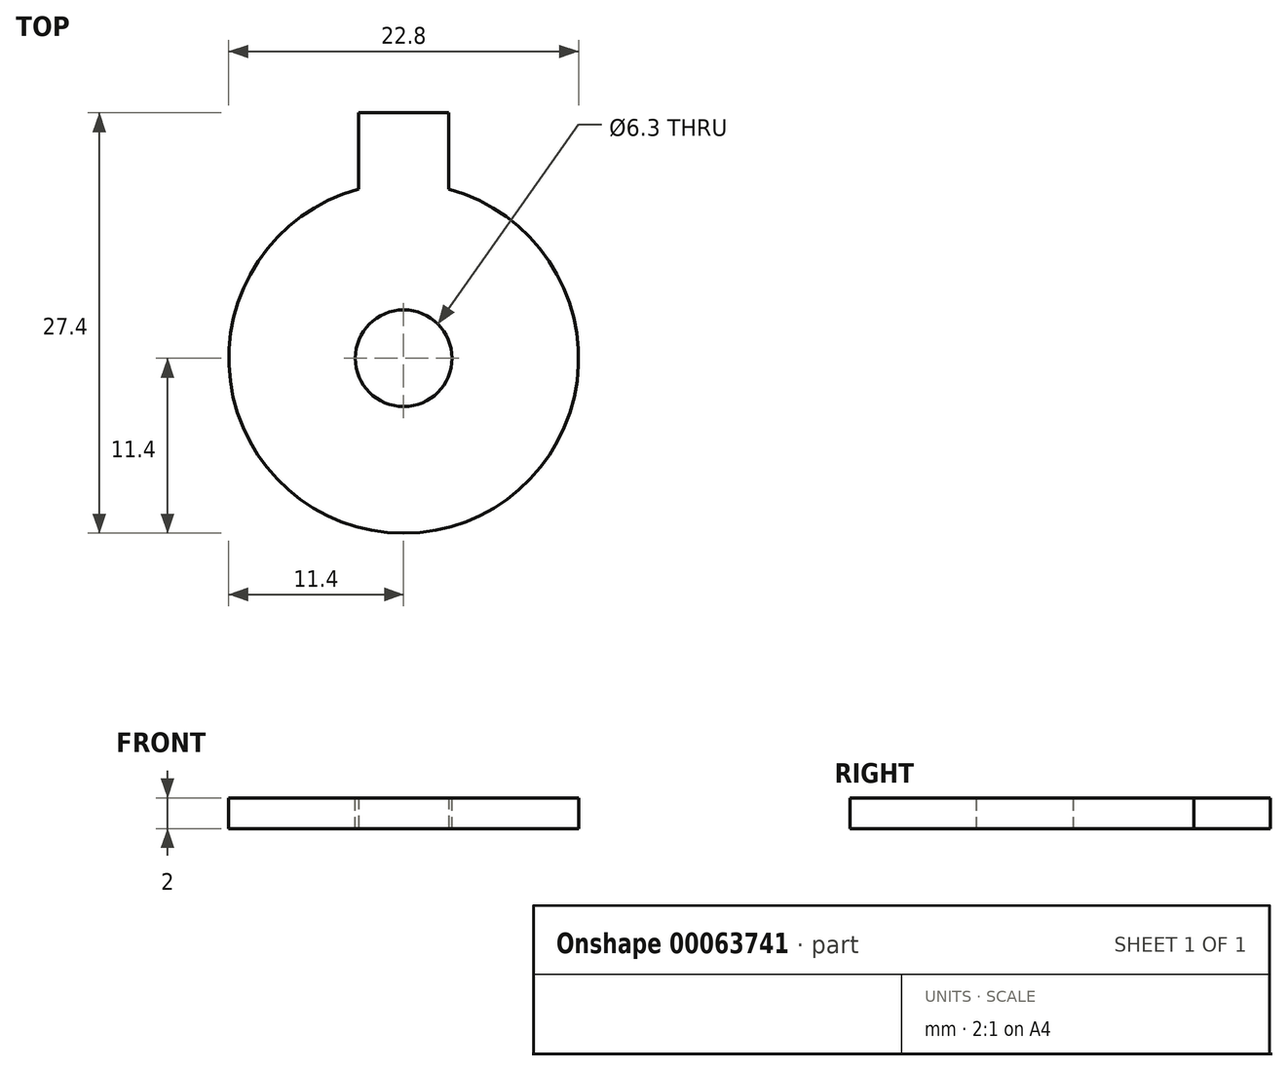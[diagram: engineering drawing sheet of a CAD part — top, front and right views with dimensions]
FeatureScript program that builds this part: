
annotation { "Feature Type Name" : "Feature", "Feature Type Description" : "" }
export const myFeature = defineFeature(function(context is Context, id is Id, definition is map)
    precondition{}
    {
        {
            var Q0;
            Q0=qCreatedBy(makeId("Top.planeOp"),FACE);
            var sketch = newSketch(context, id + "F0", { "sketchPlane" : qUnion([Q0])});
            skArc(sketch, "E0", {"start": v(-2.95, 11.01) * mm, "mid": v(0, -11.4) * mm, "end": v(2.95, 11.01) * mm});
            skLineSegment(sketch, "E1.rect.bottom", {"start": v(2.95, 16) * mm, "end": v(-2.95, 16) * mm});
            skLineSegment(sketch, "E1.rect.left", {"start": v(2.95, 16) * mm, "end": v(2.95, 11.01) * mm});
            skLineSegment(sketch, "E1.rect.right", {"start": v(-2.95, 16) * mm, "end": v(-2.95, 11.01) * mm});
            skPoint(sketch, "E1.rect.middle", {"position": v(0, 11.4) * mm});
            skPoint(sketch, "E1.rect.top.end.orphan", {"position": v(-2.95, 6.8) * mm});
            skPoint(sketch, "E2.orphan", {"position": v(2.95, 6.8) * mm});
            skSolve(sketch);
        }
        {
            var Q0;
            Q0=makeQuery(id+"F0.imprint","IMPRINT",FACE,{"disambiguationData":[TD([[makeQuery(id+"F0.imprint","IMPRINT",EDGE,{"derivedFrom":sQuery(id+"F0.wireOp",EDGE,"E0")}),1.0]])]});
            extrude(context, id + "F1", {"entities" : qUnion([Q0]), "depth" : 2 * mm});
        }
        {
            var Q0;
            Q0=makeQuery(id+"F1.opExtrude","CAP_FACE",FACE,{"disambiguationData":[OSD([sQuery(id+"F0.wireOp",EDGE,"E0"),sQuery(id+"F0.wireOp",EDGE,"E1.rect.bottom"),sQuery(id+"F0.wireOp",EDGE,"E1.rect.left"),sQuery(id+"F0.wireOp",EDGE,"E1.rect.right")])],"isStart":false});
            var sketch = newSketch(context, id + "F2", { "sketchPlane" : qUnion([Q0])});
            skCircle(sketch, "E3", {"center": v(0, 0) * mm, "radius": 3.15 * mm});
            skSolve(sketch);
        }
        {
            var Q0;
            Q0=sQuery(id+"F2.wireOp",VERTEX,"E3.center");
            var Q1;
            Q1=makeQuery(id+"F1.opExtrude","SWEPT_BODY",BODY,{"disambiguationData":[OSD([sQuery(id+"F0.wireOp",EDGE,"E0"),sQuery(id+"F0.wireOp",EDGE,"E1.rect.bottom"),sQuery(id+"F0.wireOp",EDGE,"E1.rect.left"),sQuery(id+"F0.wireOp",EDGE,"E1.rect.right")])]});
            hole(context, id + "F3", {"style" : HoleStyle.SIMPLE, "holeDiameter" : 6.3 * mm, "endStyle" : HoleEndStyle.THROUGH, "locations" : qUnion([Q0]), "scope" : qUnion([Q1])});
        }
    });
